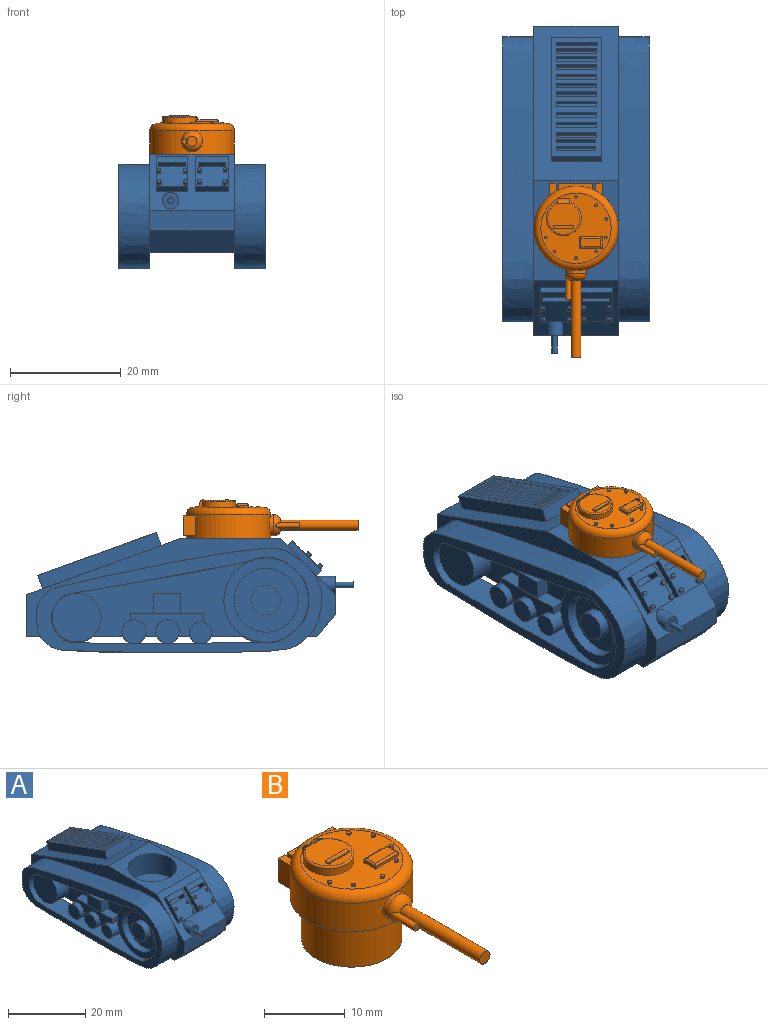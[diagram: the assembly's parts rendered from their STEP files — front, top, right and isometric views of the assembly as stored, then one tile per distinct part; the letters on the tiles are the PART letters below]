
ASSEMBLY  parts=2 mates=1
PART A: 216 faces, bbox 26.4x59x22 mm
  f0: plane 2.27x0.08mm, normal (-1,0,0), area 0.2mm2, adj f2,f14,f212,f215
  f1: plane 37.9x14.78mm, normal (-1,0,0), area 179.7mm2, adj f3,f4,f7,f14,f43,f47,f191,f198
  f2: plane 2.54x2.2mm, normal (0,0,-1), area 5.6mm2, adj f0,f192,f212,f215
  f3: extruded ~46.46x15.65mm, area 571.2mm2, adj f1,f24,f25,f26,f27,f42,f43,f44
  f4: plane 2.54x1.5mm, normal (0,-1,0), area 3.8mm2, adj f1,f191,f192,f215
  f5: plane 2.16x0.08mm, normal (-1,0,0), area 0.2mm2, adj f6,f14,f210,f212
  f6: plane 2.54x2.08mm, normal (0,0,-1), area 5.3mm2, adj f5,f192,f210,f212
  f7: plane 2.54x1.21mm, normal (0,1,0), area 3.1mm2, adj f1,f191,f192,f210
  f8: cylinder r=1.8mm len=3.6mm, axis (1,0,0), area 31.2mm2, adj f187,f188,f190,f203,f208
  f9: cylinder r=1.98mm len=3.96mm, axis (1,0,0), area 29.4mm2, adj f188,f190,f204,f207
  f10: cylinder r=2.09mm len=4.17mm, axis (1,0,0), area 35.9mm2, adj f188,f189,f190,f205,f206
  f11: plane 15.24x3.6mm, normal (0,-1,0), area 54.8mm2, adj f12,f13,f32,f185
  f12: plane 12.81x5.11mm, normal (-1,0,0), area 22mm2, adj f11,f14,f21,f32,f185
  f13: plane 12.81x5.11mm, normal (1,0,0), area 22mm2, adj f11,f14,f32,f34,f185
  f14: plane 52.5x15.24mm, normal (0,0,-1), area 800.1mm2, adj f0,f1,f5,f12,f13,f15,f22,f23
  f15: plane 15.24x7.62mm, normal (0,1,0), area 51.9mm2, adj f14,f23,f30,f33,f164,f165,f166,f167
  f16: plane 21.4x8.99mm, normal (0,0.34,0.94), area 122.2mm2, adj f69,f70,f71,f72,f73,f74,f75,f76
  f17: plane 5.92x5.3mm, normal (0,-0.71,0.7), area 37.3mm2, adj f19,f20,f56,f58,f64,f65,f66,f67
  f18: plane 5.71x5.3mm, normal (0,-0.71,0.7), area 35.8mm2, adj f53,f54,f55,f57,f59,f60,f61,f62
  f19: plane 5.92x0.9mm, normal (0,0.7,0.71), area 7.5mm2, adj f17,f32,f56,f58
  f20: plane 5.92x0.9mm, normal (0,-0.7,-0.71), area 7.5mm2, adj f17,f32,f56,f58
  f21: extruded ~51.44x18.87mm, area 685.6mm2, adj f12,f27,f30,f48
  f22: plane 37.45x15.56mm, normal (1,0,0), area 185.8mm2, adj f14,f28,f36,f39,f186,f187,f188,f189
  f23: plane 52.12x19.03mm, normal (1,0,0), area 121.7mm2, adj f14,f15,f31,f32,f33,f34
  f24: plane 5.67x1.91mm, normal (-1,0,0), area 0.8mm2, adj f3,f14,f47
  f25: plane 6.6x1.8mm, normal (-1,0,0), area 0.9mm2, adj f3,f45
  f26: plane 10x2.12mm, normal (-1,0,0), area 1.2mm2, adj f3,f44
  f27: plane 51.72x20.13mm, normal (-1,0,0), area 232.2mm2, adj f3,f21
  f28: extruded ~35.94x13.37mm, area 238.3mm2, adj f22,f29,f36,f37,f39,f40
  f29: plane 51.72x20.13mm, normal (1,0,0), area 232.2mm2, adj f28,f34,f35,f37,f40
  f30: plane 52.12x19.03mm, normal (-1,0,0), area 121.7mm2, adj f14,f15,f21,f31,f32,f33
  f31: plane 17.93x15.24mm, normal (0,0,1), area 146.6mm2, adj f23,f30,f32,f33,f51
  f32: plane 15.24x10.16mm, normal (0,-0.71,0.7), area 120.9mm2, adj f11,f12,f13,f19,f20,f23,f30,f31
  f33: plane 27.94x15.24mm, normal (0,0.34,0.94), area 248.4mm2, adj f15,f23,f30,f31,f69,f70,f71,f72
  f34: extruded ~51.44x18.87mm, area 685.6mm2, adj f13,f23,f29,f50
  f35: extruded ~36.34x5.59mm, area 204.3mm2, adj f29,f36,f37,f39,f40,f50
  f36: cylinder r=7.62mm len=14.74mm, axis (1,0,0), area 90mm2, adj f22,f28,f35,f38,f50
  f37: cylinder r=7.62mm len=15.24mm, axis (1,0,0), area 34.3mm2, adj f28,f29,f35,f38
  f38: plane 15.24x15.24mm, normal (1,0,0), area 77.5mm2, adj f36,f37,f154
  f39: cylinder r=4.45mm len=8.89mm, axis (1,0,0), area 118mm2, adj f22,f28,f35,f41,f50
  f40: cylinder r=4.45mm len=1.27mm, axis (1,0,0), area 0.8mm2, adj f28,f29,f35,f41
  f41: plane 8.89x8.89mm, normal (1,0,0), area 34.8mm2, adj f39,f40,f158
  f42: plane 15.24x15.24mm, normal (-1,0,0), area 77.5mm2, adj f3,f43,f44,f45,f160
  f43: cylinder r=7.62mm len=14.9mm, axis (1,0,0), area 110.2mm2, adj f1,f3,f42,f48
  f44: cylinder r=7.62mm len=9.94mm, axis (1,0,0), area 46.8mm2, adj f3,f26,f42
  f45: cylinder r=7.62mm len=6.45mm, axis (1,0,0), area 29.2mm2, adj f3,f25,f42
  f46: plane 8.83x8.83mm, normal (-1,0,0), area 61.2mm2, adj f3,f47
  f47: cylinder r=4.41mm len=8.83mm, axis (1,0,0), area 115.4mm2, adj f1,f3,f24,f46,f49
  f48: plane 49.2x4.34mm, normal (1,0,0), area 90.7mm2, adj f3,f14,f21,f43,f210,f215
  f49: plane 5.37x0.91mm, normal (1,0,0), area 3.3mm2, adj f14,f47
  f50: plane 49.2x4.34mm, normal (-1,0,0), area 83.7mm2, adj f14,f34,f35,f36,f39
  f51: cylinder r=6.35mm len=12.7mm, axis (0,0,1), area 253.4mm2, adj f31,f52
  f52: plane 12.7x12.7mm, normal (0,0,1), area 126.7mm2, adj f51
  f53: plane 5.71x0.9mm, normal (0,0.7,0.71), area 7.3mm2, adj f18,f32,f54,f57
  f54: plane 6.19x6.13mm, normal (-1,0,0), area 9.4mm2, adj f18,f32,f53,f55
  f55: plane 5.71x0.9mm, normal (0,-0.7,-0.71), area 7.3mm2, adj f18,f32,f54,f57
  f56: plane 6.19x6.13mm, normal (1,0,0), area 9.4mm2, adj f17,f19,f20,f32
  f57: plane 6.19x6.13mm, normal (1,0,0), area 9.4mm2, adj f18,f32,f53,f55
  f58: plane 6.19x6.13mm, normal (-1,0,0), area 9.4mm2, adj f17,f19,f20,f32
  f59: plane 4.79x1.81mm, normal (0,-0.7,-0.71), area 12.2mm2, adj f18,f60,f62,f63
  f60: plane 2.53x2.52mm, normal (1,0,0), area 2.6mm2, adj f18,f59,f61,f63
  f61: plane 4.79x1.81mm, normal (0,0.7,0.71), area 12.2mm2, adj f18,f60,f62,f63
  f62: plane 2.53x2.52mm, normal (-1,0,0), area 2.6mm2, adj f18,f59,f61,f63
  f63: plane 4.79x0.73mm, normal (0,-0.71,0.7), area 4.9mm2, adj f59,f60,f61,f62
  f64: plane 4.9x1.81mm, normal (0,-0.7,-0.71), area 12.4mm2, adj f17,f65,f67,f68
  f65: plane 2.51x2.5mm, normal (1,0,0), area 2.5mm2, adj f17,f64,f66,f68
  f66: plane 4.9x1.81mm, normal (0,0.7,0.71), area 12.4mm2, adj f17,f65,f67,f68
  f67: plane 2.51x2.5mm, normal (-1,0,0), area 2.5mm2, adj f17,f64,f66,f68
  f68: plane 4.9x0.71mm, normal (0,-0.71,0.7), area 4.9mm2, adj f64,f65,f66,f67
  f69: plane 22.27x10.17mm, normal (-1,0,0), area 57.8mm2, adj f16,f33,f70,f72
  f70: plane 8.99x2.39mm, normal (0,-0.94,0.34), area 22.8mm2, adj f16,f33,f69,f71
  f71: plane 22.27x10.17mm, normal (1,0,0), area 57.8mm2, adj f16,f33,f70,f72
  f72: plane 8.99x2.39mm, normal (0,0.94,-0.34), area 22.8mm2, adj f16,f33,f69,f71
  f73: plane 7.34x1.19mm, normal (0,-0.94,0.34), area 9.3mm2, adj f16,f74,f76,f77
  f74: plane 1.42x1.07mm, normal (1,0,0), area 0.9mm2, adj f16,f73,f75,f77
  f75: plane 7.34x1.19mm, normal (0,0.94,-0.34), area 9.3mm2, adj f16,f74,f76,f77
  f76: plane 1.42x1.07mm, normal (-1,0,0), area 0.9mm2, adj f16,f73,f75,f77
  f77: plane 7.34x0.64mm, normal (0,0.34,0.94), area 5mm2, adj f73,f74,f75,f76
  f78: plane 7.14x1.19mm, normal (0,-0.94,0.34), area 9.1mm2, adj f16,f79,f81,f82
  f79: plane 1.45x1.14mm, normal (1,0,0), area 1mm2, adj f16,f78,f80,f82
  f80: plane 7.14x1.19mm, normal (0,0.94,-0.34), area 9.1mm2, adj f16,f79,f81,f82
  f81: plane 1.45x1.14mm, normal (-1,0,0), area 1mm2, adj f16,f78,f80,f82
  f82: plane 7.14x0.71mm, normal (0,0.34,0.94), area 5.4mm2, adj f78,f79,f80,f81
  f83: plane 7.25x1.19mm, normal (0,-0.94,0.34), area 9.2mm2, adj f16,f84,f86,f87
  f84: plane 1.51x1.31mm, normal (1,0,0), area 1.2mm2, adj f16,f83,f85,f87
  f85: plane 7.25x1.19mm, normal (0,0.94,-0.34), area 9.2mm2, adj f16,f84,f86,f87
  f86: plane 1.51x1.31mm, normal (-1,0,0), area 1.2mm2, adj f16,f83,f85,f87
  f87: plane 7.25x0.87mm, normal (0,0.34,0.94), area 6.7mm2, adj f83,f84,f85,f86
  f88: plane 7.09x1.19mm, normal (0,-0.94,0.34), area 9mm2, adj f16,f89,f91,f92
  f89: plane 1.4x0.99mm, normal (1,0,0), area 0.8mm2, adj f16,f88,f90,f92
  f90: plane 7.09x1.19mm, normal (0,0.94,-0.34), area 9mm2, adj f16,f89,f91,f92
  f91: plane 1.4x0.99mm, normal (-1,0,0), area 0.8mm2, adj f16,f88,f90,f92
  f92: plane 7.09x0.56mm, normal (0,0.34,0.94), area 4.2mm2, adj f88,f89,f90,f91
  f93: plane 7.36x1.19mm, normal (0,-0.94,0.34), area 9.3mm2, adj f16,f94,f96,f97
  f94: plane 1.53x1.36mm, normal (1,0,0), area 1.3mm2, adj f16,f93,f95,f97
  f95: plane 7.36x1.19mm, normal (0,0.94,-0.34), area 9.3mm2, adj f16,f94,f96,f97
  f96: plane 1.53x1.36mm, normal (-1,0,0), area 1.3mm2, adj f16,f93,f95,f97
  f97: plane 7.36x0.93mm, normal (0,0.34,0.94), area 7.3mm2, adj f93,f94,f95,f96
  f98: plane 7.36x1.19mm, normal (0,-0.94,0.34), area 9.3mm2, adj f16,f99,f101,f102
  f99: plane 1.53x1.36mm, normal (1,0,0), area 1.3mm2, adj f16,f98,f100,f102
  f100: plane 7.36x1.19mm, normal (0,0.94,-0.34), area 9.3mm2, adj f16,f99,f101,f102
  f101: plane 1.53x1.36mm, normal (-1,0,0), area 1.3mm2, adj f16,f98,f100,f102
  f102: plane 7.36x0.93mm, normal (0,0.34,0.94), area 7.3mm2, adj f98,f99,f100,f101
  f103: plane 7.36x1.19mm, normal (0,-0.94,0.34), area 9.3mm2, adj f16,f104,f106,f107
  f104: plane 1.53x1.36mm, normal (1,0,0), area 1.3mm2, adj f16,f103,f105,f107
  f105: plane 7.36x1.19mm, normal (0,0.94,-0.34), area 9.3mm2, adj f16,f104,f106,f107
  f106: plane 1.53x1.36mm, normal (-1,0,0), area 1.3mm2, adj f16,f103,f105,f107
  f107: plane 7.36x0.93mm, normal (0,0.34,0.94), area 7.3mm2, adj f103,f104,f105,f106
  f108: plane 7.36x1.19mm, normal (0,-0.94,0.34), area 9.3mm2, adj f16,f109,f111,f112
  f109: plane 1.53x1.36mm, normal (1,0,0), area 1.3mm2, adj f16,f108,f110,f112
  f110: plane 7.36x1.19mm, normal (0,0.94,-0.34), area 9.3mm2, adj f16,f109,f111,f112
  f111: plane 1.53x1.36mm, normal (-1,0,0), area 1.3mm2, adj f16,f108,f110,f112
  f112: plane 7.36x0.93mm, normal (0,0.34,0.94), area 7.3mm2, adj f108,f109,f110,f111
  f113: plane 7.31x1.19mm, normal (0,-0.94,0.34), area 9.3mm2, adj f16,f114,f116,f117
  f114: plane 1.49x1.25mm, normal (1,0,0), area 1.1mm2, adj f16,f113,f115,f117
  f115: plane 7.31x1.19mm, normal (0,0.94,-0.34), area 9.3mm2, adj f16,f114,f116,f117
  f116: plane 1.49x1.25mm, normal (-1,0,0), area 1.1mm2, adj f16,f113,f115,f117
  f117: plane 7.31x0.82mm, normal (0,0.34,0.94), area 6.4mm2, adj f113,f114,f115,f116
  f118: plane 7.31x1.19mm, normal (0,-0.94,0.34), area 9.3mm2, adj f16,f119,f121,f122
  f119: plane 1.53x1.36mm, normal (1,0,0), area 1.3mm2, adj f16,f118,f120,f122
  f120: plane 7.31x1.19mm, normal (0,0.94,-0.34), area 9.3mm2, adj f16,f119,f121,f122
  f121: plane 1.53x1.36mm, normal (-1,0,0), area 1.3mm2, adj f16,f118,f120,f122
  f122: plane 7.31x0.93mm, normal (0,0.34,0.94), area 7.2mm2, adj f118,f119,f120,f121
  f123: plane 7.31x1.19mm, normal (0,-0.94,0.34), area 9.3mm2, adj f16,f124,f126,f127
  f124: plane 1.49x1.25mm, normal (1,0,0), area 1.1mm2, adj f16,f123,f125,f127
  f125: plane 7.31x1.19mm, normal (0,0.94,-0.34), area 9.3mm2, adj f16,f124,f126,f127
  f126: plane 1.49x1.25mm, normal (-1,0,0), area 1.1mm2, adj f16,f123,f125,f127
  f127: plane 7.31x0.82mm, normal (0,0.34,0.94), area 6.4mm2, adj f123,f124,f125,f126
  f128: plane 7.25x1.19mm, normal (0,-0.94,0.34), area 9.2mm2, adj f16,f129,f131,f132
  f129: plane 1.49x1.25mm, normal (1,0,0), area 1.1mm2, adj f16,f128,f130,f132
  f130: plane 7.25x1.19mm, normal (0,0.94,-0.34), area 9.2mm2, adj f16,f129,f131,f132
  f131: plane 1.49x1.25mm, normal (-1,0,0), area 1.1mm2, adj f16,f128,f130,f132
  f132: plane 7.25x0.82mm, normal (0,0.34,0.94), area 6.3mm2, adj f128,f129,f130,f131
  f133: plane 7.31x1.19mm, normal (0,-0.94,0.34), area 9.3mm2, adj f16,f134,f136,f137
  f134: plane 1.47x1.2mm, normal (1,0,0), area 1mm2, adj f16,f133,f135,f137
  f135: plane 7.31x1.19mm, normal (0,0.94,-0.34), area 9.3mm2, adj f16,f134,f136,f137
  f136: plane 1.47x1.2mm, normal (-1,0,0), area 1mm2, adj f16,f133,f135,f137
  f137: plane 7.31x0.76mm, normal (0,0.34,0.94), area 5.9mm2, adj f133,f134,f135,f136
  f138: cylinder r=0.37mm len=0.97mm, axis (0,0.71,-0.7), area 1.5mm2, adj f18,f139
  f139: plane 0.74x0.53mm, normal (0,-0.71,0.7), area 0.4mm2, adj f138
  f140: cylinder r=0.38mm len=0.98mm, axis (0,0.71,-0.7), area 1.5mm2, adj f18,f141
  f141: plane 0.76x0.54mm, normal (0,-0.71,0.7), area 0.4mm2, adj f140
  f142: cylinder r=0.4mm len=1.01mm, axis (0,0.71,-0.7), area 1.6mm2, adj f17,f143
  f143: plane 0.79x0.56mm, normal (0,-0.71,0.7), area 0.5mm2, adj f142
  f144: cylinder r=0.42mm len=1.05mm, axis (0,0.71,-0.7), area 1.7mm2, adj f17,f145
  f145: plane 0.84x0.6mm, normal (0,-0.71,0.7), area 0.6mm2, adj f144
  f146: cylinder r=0.36mm len=0.96mm, axis (0,0.71,-0.7), area 1.4mm2, adj f18,f147
  f147: plane 0.72x0.51mm, normal (0,-0.71,0.7), area 0.4mm2, adj f146
  f148: cylinder r=0.38mm len=0.99mm, axis (0,0.71,-0.7), area 1.5mm2, adj f18,f149
  f149: plane 0.77x0.55mm, normal (0,-0.71,0.7), area 0.5mm2, adj f148
  f150: cylinder r=0.36mm len=0.96mm, axis (0,0.71,-0.7), area 1.4mm2, adj f17,f151
  f151: plane 0.72x0.51mm, normal (0,-0.71,0.7), area 0.4mm2, adj f150
  f152: cylinder r=0.35mm len=0.95mm, axis (0,0.71,-0.7), area 1.4mm2, adj f17,f153
  f153: plane 0.7x0.5mm, normal (0,-0.71,0.7), area 0.4mm2, adj f152
  f154: cylinder r=5.78mm len=11.56mm, axis (1,0,0), area 23.1mm2, adj f38,f155
  f155: plane 11.56x11.56mm, normal (1,0,0), area 83.8mm2, adj f154,f156
  f156: cylinder r=2.59mm len=5.18mm, axis (1,0,0), area 31mm2, adj f155,f157
  f157: plane 5.18x5.18mm, normal (1,0,0), area 21.1mm2, adj f156
  f158: cylinder r=2.95mm len=5.89mm, axis (1,0,0), area 11.8mm2, adj f41,f159
  f159: plane 5.89x5.89mm, normal (1,0,0), area 27.3mm2, adj f158
  f160: cylinder r=5.77mm len=11.55mm, axis (-1,0,0), area 69.1mm2, adj f42,f161
  f161: plane 11.55x11.55mm, normal (-1,0,0), area 83mm2, adj f160,f162
  f162: cylinder r=2.63mm len=5.26mm, axis (1,0,0), area 31.5mm2, adj f161,f163
  f163: plane 5.26x5.26mm, normal (-1,0,0), area 21.7mm2, adj f162
  f164: plane 5.08x2.54mm, normal (-1,0,0), area 12.9mm2, adj f15,f165,f167,f168
  f165: plane 12.64x2.54mm, normal (0,0,1), area 32.1mm2, adj f15,f164,f166,f168
  f166: plane 5.08x2.54mm, normal (1,0,0), area 12.9mm2, adj f15,f165,f167,f168
  f167: plane 12.64x2.54mm, normal (0,0,-1), area 32.1mm2, adj f15,f164,f166,f168
  f168: plane 12.64x5.08mm, normal (0,1,0), area 29.7mm2, adj f164,f165,f166,f167,f169,f171,f172,f173
  f169: cylinder r=1.64mm len=3.28mm, axis (0,-1,0), area 26.2mm2, adj f168,f170
  f170: plane 3.28x3.28mm, normal (0,1,0), area 8.5mm2, adj f169
  f171: plane 3.38x2.54mm, normal (0,0,1), area 8.6mm2, adj f168,f172,f174,f175
  f172: plane 3.97x2.54mm, normal (1,0,0), area 10.1mm2, adj f168,f171,f173,f175
  f173: plane 3.38x2.54mm, normal (0,0,-1), area 8.6mm2, adj f168,f172,f174,f175
  f174: plane 3.97x2.54mm, normal (-1,0,0), area 10.1mm2, adj f168,f171,f173,f175
  f175: plane 3.97x3.38mm, normal (0,1,0), area 13.4mm2, adj f171,f172,f173,f174
  f176: plane 3.2x2.54mm, normal (0,0,1), area 8.1mm2, adj f168,f177,f179,f180
  f177: plane 3.97x2.54mm, normal (1,0,0), area 10.1mm2, adj f168,f176,f178,f180
  f178: plane 3.2x2.54mm, normal (0,0,-1), area 8.1mm2, adj f168,f177,f179,f180
  f179: plane 3.97x2.54mm, normal (-1,0,0), area 10.1mm2, adj f168,f176,f178,f180
  f180: plane 3.97x3.2mm, normal (0,1,0), area 12.7mm2, adj f176,f177,f178,f179
  f181: cylinder r=1.5mm len=3.26mm, axis (0,1,0), area 16.8mm2, adj f32,f182
  f182: plane 3x3mm, normal (0,-1,0), area 6.2mm2, adj f181,f183
  f183: cylinder r=0.52mm len=3.15mm, axis (0,1,0), area 10.2mm2, adj f182,f184
  f184: plane 1.03x1.03mm, normal (0,-1,0), area 0.8mm2, adj f183
  f185: plane 15.24x4.02mm, normal (0,-0.77,-0.64), area 80.1mm2, adj f11,f12,f13,f14
  f186: plane 13.19x2.54mm, normal (0,0,1), area 33.5mm2, adj f22,f187,f189,f190
  f187: plane 4.12x2.54mm, normal (0,-1,0), area 7.1mm2, adj f8,f22,f186,f188,f190,f203
  f188: plane 13.19x2.54mm, normal (0,0,-1), area 20.1mm2, adj f8,f9,f10,f22,f187,f189,f190,f203
  f189: plane 4.12x2.54mm, normal (0,1,0), area 6.4mm2, adj f10,f22,f186,f188,f190,f205
  f190: plane 13.19x4.12mm, normal (1,0,0), area 33.4mm2, adj f8,f9,f10,f186,f187,f188,f189
  f191: plane 13.19x2.54mm, normal (0,0,1), area 33.5mm2, adj f1,f4,f7,f192
  f192: plane 13.19x4.12mm, normal (-1,0,0), area 30.1mm2, adj f2,f4,f6,f7,f191,f210,f212,f215
  f193: plane 3.47x2.54mm, normal (0,-1,0), area 8.8mm2, adj f22,f194,f196,f197
  f194: plane 4.92x2.54mm, normal (0,0,-1), area 12.5mm2, adj f22,f193,f195,f197
  f195: plane 3.47x2.54mm, normal (0,1,0), area 8.8mm2, adj f22,f194,f196,f197
  f196: plane 4.92x2.54mm, normal (0,0,1), area 12.5mm2, adj f22,f193,f195,f197
  f197: plane 4.92x3.47mm, normal (1,0,0), area 17.1mm2, adj f193,f194,f195,f196
  f198: plane 3.47x2.54mm, normal (0,-1,0), area 8.8mm2, adj f1,f199,f201,f202
  f199: plane 4.92x2.54mm, normal (0,0,-1), area 12.5mm2, adj f1,f198,f200,f202
  f200: plane 3.47x2.54mm, normal (0,1,0), area 8.8mm2, adj f1,f199,f201,f202
  f201: plane 4.92x2.54mm, normal (0,0,1), area 12.5mm2, adj f1,f198,f200,f202
  f202: plane 4.92x3.47mm, normal (-1,0,0), area 17.1mm2, adj f198,f199,f200,f201
  f203: plane 3.52x3.47mm, normal (-1,0,0), area 5.2mm2, adj f8,f187,f188
  f204: plane 3.69x1.27mm, normal (-1,0,0), area 3.4mm2, adj f9,f188
  f205: plane 4.03x4.03mm, normal (-1,0,0), area 6.6mm2, adj f10,f188,f189
  f206: plane 4.17x4.17mm, normal (1,0,0), area 13.7mm2, adj f10
  f207: plane 3.96x3.96mm, normal (1,0,0), area 12.3mm2, adj f9
  f208: plane 3.6x3.6mm, normal (1,0,0), area 10.2mm2, adj f8
  f209: plane 4.34x4.3mm, normal (-1,0,0), area 14.8mm2, adj f3,f210
  f210: cylinder r=2.17mm len=4.34mm, axis (1,0,0), area 38.5mm2, adj f1,f3,f5,f6,f7,f48,f192,f209
  f211: plane 3.79x1.14mm, normal (1,0,0), area 3.1mm2, adj f14,f212
  f212: cylinder r=2.14mm len=4.27mm, axis (1,0,0), area 32.1mm2, adj f0,f2,f5,f6,f192,f211,f213
  f213: plane 4.27x4.27mm, normal (-1,0,0), area 14.3mm2, adj f212
  f214: plane 3.99x3.91mm, normal (-1,0,0), area 12.4mm2, adj f3,f215
  f215: cylinder r=1.99mm len=4.01mm, axis (1,0,0), area 34.8mm2, adj f0,f1,f2,f3,f4,f48,f192,f214
PART B: 115 faces, bbox 16.5x31.6x13.5 mm
  f0: plane 6.16x3.57mm, normal (0,1,0), area 14.1mm2, adj f56,f57,f58,f59,f65,f66,f67,f68
  f1: cylinder r=7.62mm len=15.24mm, axis (0,0,-1), area 162.5mm2, adj f5,f6,f7,f51,f52,f53,f54,f56
  f2: plane 12.7x12.7mm, normal (0,0,1), area 84.6mm2, adj f6,f13,f15,f16,f17,f26,f27,f28
  f3: cylinder r=6.22mm len=12.45mm, axis (0,0,-1), area 248.3mm2, adj f4,f5
  f4: plane 12.45x12.45mm, normal (0,0,-1), area 121.7mm2, adj f3
  f5: plane 15.24x15.24mm, normal (0,0,-1), area 60.8mm2, adj f1,f3
  f6: torus R=6.35mm, axis (0,0,1), area 89.7mm2, adj f1,f2
  f7: cylinder r=1.9mm len=3.8mm, axis (0,1,0), area 7.8mm2, adj f1,f12
  f8: cylinder r=0.9mm len=13.97mm, axis (0,1,0), area 78.9mm2, adj f9,f12
  f9: plane 1.8x1.8mm, normal (0,-1,0), area 2.5mm2, adj f8
  f10: cylinder r=0.47mm len=4.26mm, axis (0,1,0), area 11mm2, adj f11,f12
  f11: plane 0.93x0.93mm, normal (0,-1,0), area 0.7mm2, adj f10
  f12: torus R=0.63mm, axis (0,-1,0), area 15.7mm2, adj f7,f8,f10
  f13: cylinder r=3.15mm len=6.3mm, axis (0,0,-1), area 17.9mm2, adj f2,f15,f16,f19
  f14: plane 5.79x5.62mm, normal (0,0,1), area 23.8mm2, adj f15,f16,f18,f19,f20,f21,f22,f23
  f15: plane 1.52x0.84mm, normal (1,0,0), area 0.6mm2, adj f2,f13,f14,f17,f18,f19,f25
  f16: plane 1.52x0.84mm, normal (-1,0,0), area 0.7mm2, adj f2,f13,f14,f17,f18,f19,f25
  f17: plane 2.17x0.33mm, normal (0,1,0), area 0.7mm2, adj f2,f15,f16,f25
  f18: plane 2.17x0.25mm, normal (0,-1,0), area 0.6mm2, adj f14,f15,f16,f25
  f19: torus R=2.9mm, axis (0,0,1), area 6.8mm2, adj f13,f14,f15,f16
  f20: plane 0.6x0.25mm, normal (-1,0,0), area 0.2mm2, adj f14,f21,f23,f24
  f21: plane 3.63x0.25mm, normal (0,-1,0), area 0.9mm2, adj f14,f20,f22,f24
  f22: plane 0.6x0.25mm, normal (1,0,0), area 0.2mm2, adj f14,f21,f23,f24
  f23: plane 3.63x0.25mm, normal (0,1,0), area 0.9mm2, adj f14,f20,f22,f24
  f24: plane 3.63x0.6mm, normal (0,0,1), area 2.2mm2, adj f20,f21,f22,f23
  f25: cylinder r=1.27mm len=2.17mm, axis (1,0,0), area 3.4mm2, adj f15,f16,f17,f18
  f26: plane 2.06x0.38mm, normal (-1,0,0), area 0.8mm2, adj f2,f27,f29,f31
  f27: plane 4.08x0.38mm, normal (0,-1,0), area 1.6mm2, adj f2,f26,f28,f32
  f28: plane 2.06x0.38mm, normal (1,0,0), area 0.8mm2, adj f2,f27,f29,f34
  f29: plane 4.08x0.38mm, normal (0,1,0), area 1.6mm2, adj f2,f26,f28,f33
  f30: plane 3.57x1.56mm, normal (0,0,1), area 5.6mm2, adj f31,f32,f33,f34
  f31: cylinder r=0.25mm len=2.06mm, axis (0,1,0), area 0.7mm2, adj f26,f30,f32,f33
  f32: cylinder r=0.25mm len=4.08mm, axis (-1,0,0), area 1.6mm2, adj f27,f30,f31,f34
  f33: cylinder r=0.25mm len=4.08mm, axis (1,0,0), area 1.6mm2, adj f29,f30,f31,f34
  f34: cylinder r=0.25mm len=2.06mm, axis (0,-1,0), area 0.7mm2, adj f28,f30,f32,f33
  f35: cylinder r=0.26mm len=0.51mm, axis (0,0,-1), area 0.4mm2, adj f2,f36
  f36: plane 0.51x0.51mm, normal (0,0,1), area 0.2mm2, adj f35
  f37: cylinder r=0.23mm len=0.47mm, axis (0,0,-1), area 0.4mm2, adj f2,f38
  f38: plane 0.47x0.47mm, normal (0,0,1), area 0.2mm2, adj f37
  f39: cylinder r=0.25mm len=0.5mm, axis (0,0,-1), area 0.4mm2, adj f2,f40
  f40: plane 0.5x0.5mm, normal (0,0,1), area 0.2mm2, adj f39
  f41: cylinder r=0.24mm len=0.49mm, axis (0,0,-1), area 0.4mm2, adj f2,f42
  f42: plane 0.49x0.49mm, normal (0,0,1), area 0.2mm2, adj f41
  f43: cylinder r=0.25mm len=0.5mm, axis (0,0,-1), area 0.4mm2, adj f2,f44
  f44: plane 0.5x0.5mm, normal (0,0,1), area 0.2mm2, adj f43
  f45: cylinder r=0.27mm len=0.54mm, axis (0,0,-1), area 0.4mm2, adj f2,f46
  f46: plane 0.54x0.54mm, normal (0,0,1), area 0.2mm2, adj f45
  f47: cylinder r=0.25mm len=0.49mm, axis (0,0,-1), area 0.4mm2, adj f2,f48
  f48: plane 0.49x0.49mm, normal (0,0,1), area 0.2mm2, adj f47
  f49: cylinder r=0.24mm len=0.48mm, axis (0,0,-1), area 0.4mm2, adj f2,f50
  f50: plane 0.48x0.48mm, normal (0,0,1), area 0.2mm2, adj f49
  f51: plane 3.66x2.15mm, normal (1,0,0), area 7.9mm2, adj f1,f53,f54,f55
  f52: plane 3.66x1.37mm, normal (-1,0,0), area 5mm2, adj f1,f53,f54,f55
  f53: plane 2.15x1.2mm, normal (0,0,1), area 2.1mm2, adj f1,f51,f52,f55
  f54: plane 2.15x1.2mm, normal (0,0,-1), area 2.1mm2, adj f1,f51,f52,f55
  f55: plane 3.66x1.2mm, normal (0,1,0), area 4.4mm2, adj f51,f52,f53,f54
  f56: plane 3.57x1.14mm, normal (1,0,0), area 4.1mm2, adj f0,f1,f58,f59
  f57: plane 3.57x1.18mm, normal (-1,0,0), area 4.2mm2, adj f0,f1,f58,f59
  f58: plane 6.16x1.18mm, normal (0,0,1), area 4.4mm2, adj f0,f1,f56,f57
  f59: plane 6.16x1.18mm, normal (0,0,-1), area 4.4mm2, adj f0,f1,f56,f57
  f60: plane 3.53x1.41mm, normal (1,0,0), area 5mm2, adj f1,f62,f63,f64
  f61: plane 3.53x2.19mm, normal (-1,0,0), area 7.7mm2, adj f1,f62,f63,f64
  f62: plane 2.19x1.17mm, normal (0,0,1), area 2.1mm2, adj f1,f60,f61,f64
  f63: plane 2.19x1.17mm, normal (0,0,-1), area 2.1mm2, adj f1,f60,f61,f64
  f64: plane 3.53x1.17mm, normal (0,1,0), area 4.1mm2, adj f60,f61,f62,f63
  f65: plane 0.25x0.23mm, normal (0,0,-1), area 0.1mm2, adj f0,f66,f68,f69
  f66: plane 2.98x0.25mm, normal (-1,0,0), area 0.8mm2, adj f0,f65,f67,f69
  f67: plane 0.25x0.23mm, normal (0,0,1), area 0.1mm2, adj f0,f66,f68,f69
  f68: plane 2.98x0.25mm, normal (1,0,0), area 0.8mm2, adj f0,f65,f67,f69
  f69: plane 2.98x0.23mm, normal (0,1,0), area 0.7mm2, adj f65,f66,f67,f68
  f70: plane 0.26x0.25mm, normal (0,0,-1), area 0.1mm2, adj f0,f71,f73,f74
  f71: plane 2.98x0.25mm, normal (-1,0,0), area 0.8mm2, adj f0,f70,f72,f74
  f72: plane 0.26x0.25mm, normal (0,0,1), area 0.1mm2, adj f0,f71,f73,f74
  f73: plane 2.98x0.25mm, normal (1,0,0), area 0.8mm2, adj f0,f70,f72,f74
  f74: plane 2.98x0.26mm, normal (0,1,0), area 0.8mm2, adj f70,f71,f72,f73
  f75: plane 0.28x0.25mm, normal (0,0,-1), area 0.1mm2, adj f0,f76,f78,f79
  f76: plane 2.98x0.25mm, normal (-1,0,0), area 0.8mm2, adj f0,f75,f77,f79
  f77: plane 0.28x0.25mm, normal (0,0,1), area 0.1mm2, adj f0,f76,f78,f79
  f78: plane 2.98x0.25mm, normal (1,0,0), area 0.8mm2, adj f0,f75,f77,f79
  f79: plane 2.98x0.28mm, normal (0,1,0), area 0.8mm2, adj f75,f76,f77,f78
  f80: plane 0.31x0.25mm, normal (0,0,-1), area 0.1mm2, adj f0,f81,f83,f84
  f81: plane 2.98x0.25mm, normal (-1,0,0), area 0.8mm2, adj f0,f80,f82,f84
  f82: plane 0.31x0.25mm, normal (0,0,1), area 0.1mm2, adj f0,f81,f83,f84
  f83: plane 2.98x0.25mm, normal (1,0,0), area 0.8mm2, adj f0,f80,f82,f84
  f84: plane 2.98x0.31mm, normal (0,1,0), area 0.9mm2, adj f80,f81,f82,f83
  f85: plane 0.28x0.25mm, normal (0,0,-1), area 0.1mm2, adj f0,f86,f88,f89
  f86: plane 2.98x0.25mm, normal (-1,0,0), area 0.8mm2, adj f0,f85,f87,f89
  f87: plane 0.28x0.25mm, normal (0,0,1), area 0.1mm2, adj f0,f86,f88,f89
  f88: plane 2.98x0.25mm, normal (1,0,0), area 0.8mm2, adj f0,f85,f87,f89
  f89: plane 2.98x0.28mm, normal (0,1,0), area 0.8mm2, adj f85,f86,f87,f88
  f90: plane 0.26x0.25mm, normal (0,0,-1), area 0.1mm2, adj f0,f91,f93,f94
  f91: plane 2.98x0.25mm, normal (-1,0,0), area 0.8mm2, adj f0,f90,f92,f94
  f92: plane 0.26x0.25mm, normal (0,0,1), area 0.1mm2, adj f0,f91,f93,f94
  f93: plane 2.98x0.25mm, normal (1,0,0), area 0.8mm2, adj f0,f90,f92,f94
  f94: plane 2.98x0.26mm, normal (0,1,0), area 0.8mm2, adj f90,f91,f92,f93
  f95: plane 0.26x0.25mm, normal (0,0,-1), area 0.1mm2, adj f0,f96,f98,f99
  f96: plane 2.98x0.25mm, normal (-1,0,0), area 0.8mm2, adj f0,f95,f97,f99
  f97: plane 0.26x0.25mm, normal (0,0,1), area 0.1mm2, adj f0,f96,f98,f99
  f98: plane 2.98x0.25mm, normal (1,0,0), area 0.8mm2, adj f0,f95,f97,f99
  f99: plane 2.98x0.26mm, normal (0,1,0), area 0.8mm2, adj f95,f96,f97,f98
  f100: plane 0.26x0.25mm, normal (0,0,-1), area 0.1mm2, adj f0,f101,f103,f104
  f101: plane 2.96x0.25mm, normal (-1,0,0), area 0.8mm2, adj f0,f100,f102,f104
  f102: plane 0.26x0.25mm, normal (0,0,1), area 0.1mm2, adj f0,f101,f103,f104
  f103: plane 2.96x0.25mm, normal (1,0,0), area 0.8mm2, adj f0,f100,f102,f104
  f104: plane 2.96x0.26mm, normal (0,1,0), area 0.8mm2, adj f100,f101,f102,f103
  f105: plane 0.25x0.23mm, normal (0,0,-1), area 0.1mm2, adj f0,f106,f108,f109
  f106: plane 2.93x0.25mm, normal (-1,0,0), area 0.7mm2, adj f0,f105,f107,f109
  f107: plane 0.25x0.23mm, normal (0,0,1), area 0.1mm2, adj f0,f106,f108,f109
  f108: plane 2.93x0.25mm, normal (1,0,0), area 0.7mm2, adj f0,f105,f107,f109
  f109: plane 2.93x0.23mm, normal (0,1,0), area 0.7mm2, adj f105,f106,f107,f108
  f110: plane 0.28x0.25mm, normal (0,0,-1), area 0.1mm2, adj f0,f111,f113,f114
  f111: plane 2.93x0.25mm, normal (-1,0,0), area 0.7mm2, adj f0,f110,f112,f114
  f112: plane 0.28x0.25mm, normal (0,0,1), area 0.1mm2, adj f0,f111,f113,f114
  f113: plane 2.93x0.25mm, normal (1,0,0), area 0.7mm2, adj f0,f110,f112,f114
  f114: plane 2.93x0.28mm, normal (0,1,0), area 0.8mm2, adj f110,f111,f112,f113
PLACE A t=(-3.99,0.06,-9.24)mm
PLACE B t=(-3.99,-8.55,4.73)mm
MATE fastened B.f3 <-> A.f51  axis (0,0,-1) through (-3.99,-8.55,4.73)mm
